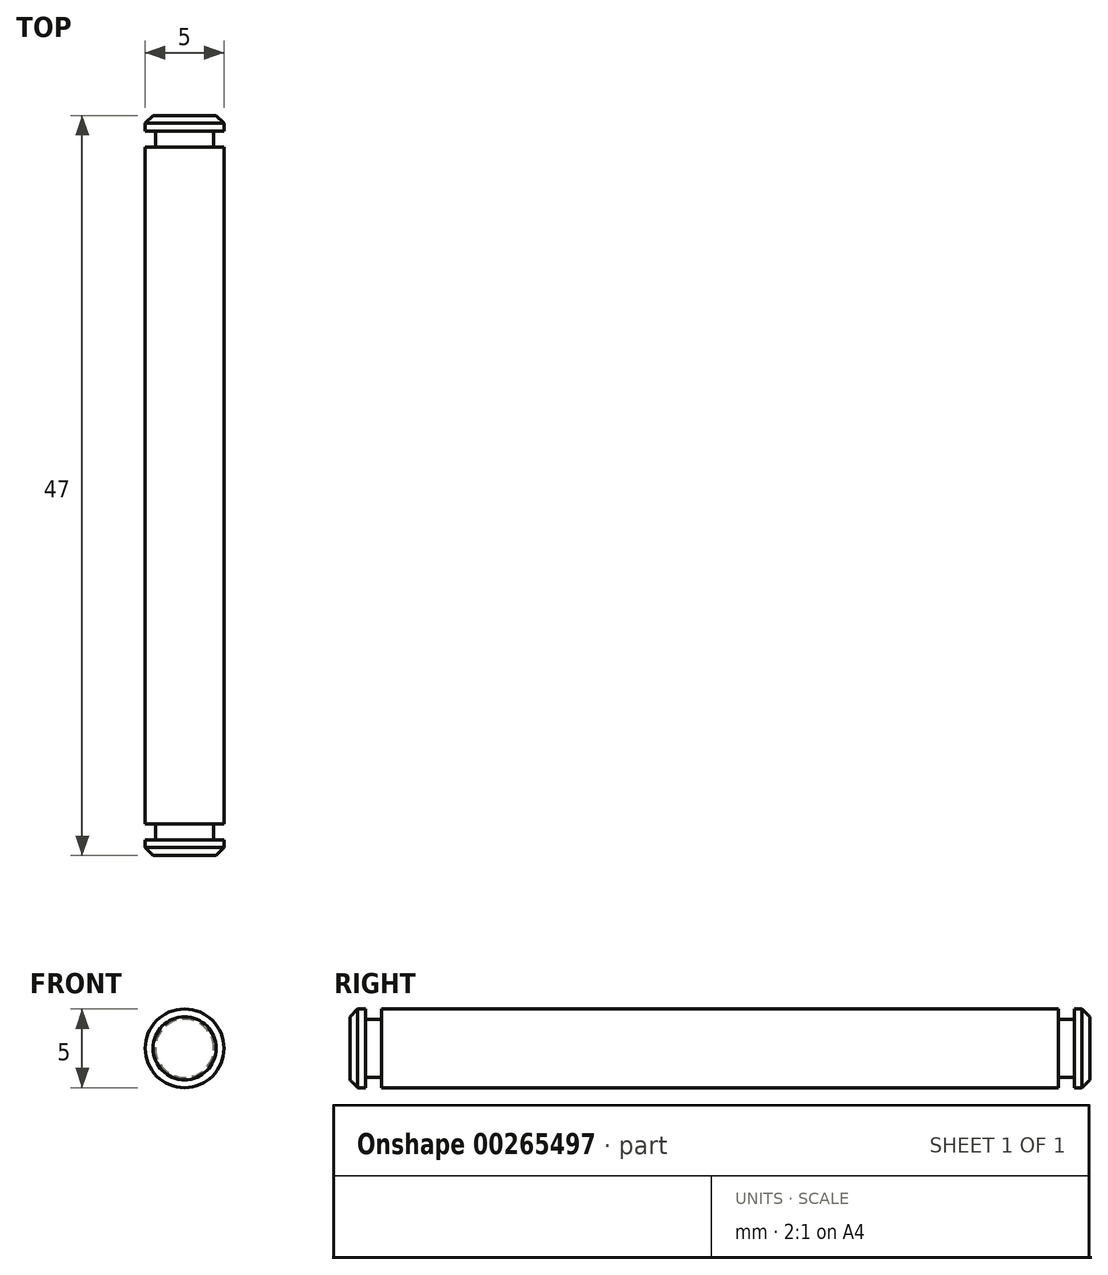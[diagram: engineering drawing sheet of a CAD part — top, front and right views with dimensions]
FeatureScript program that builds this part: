
annotation { "Feature Type Name" : "Feature", "Feature Type Description" : "" }
export const myFeature = defineFeature(function(context is Context, id is Id, definition is map)
    precondition{}
    {
        {
            var Q0;
            Q0=qCreatedBy(makeId("Front.planeOp"),FACE);
            var sketch = newSketch(context, id + "F0", { "sketchPlane" : qUnion([Q0])});
            skCircle(sketch, "E0", {"center": v(0, 0) * mm, "radius": 2.5 * mm});
            skSolve(sketch);
        }
        {
            var Q0;
            Q0=makeQuery(id+"F0.imprint","IMPRINT",FACE,{"disambiguationData":[TD([[makeQuery(id+"F0.imprint","IMPRINT",EDGE,{"derivedFrom":sQuery(id+"F0.wireOp",EDGE,"E0")}),1.0]])]});
            extrude(context, id + "F1", {"entities" : qUnion([Q0]), "depth" : 1 * mm});
        }
        {
            var Q0;
            Q0=makeQuery(id+"F1.opExtrude","CAP_FACE",FACE,{"disambiguationData":[OSD([sQuery(id+"F0.wireOp",EDGE,"E0")])],"isStart":false});
            var sketch = newSketch(context, id + "F2", { "sketchPlane" : qUnion([Q0])});
            skCircle(sketch, "E1", {"center": v(0, 0) * mm, "radius": 1.85 * mm});
            skSolve(sketch);
        }
        {
            var Q0;
            Q0=makeQuery(id+"F2.imprint","IMPRINT",FACE,{"disambiguationData":[TD([[makeQuery(id+"F2.imprint","IMPRINT",EDGE,{"derivedFrom":sQuery(id+"F2.wireOp",EDGE,"E1")}),1.0]])]});
            extrude(context, id + "F3", {"entities" : qUnion([Q0]), "operationType" : NewBodyOperationType.ADD, "depth" : 1 * mm});
        }
        {
            var Q0;
            Q0=makeQuery(id+"F3.opExtrude","CAP_FACE",FACE,{"disambiguationData":[OSD([sQuery(id+"F2.wireOp",EDGE,"E1")])],"isStart":false});
            var sketch = newSketch(context, id + "F4", { "sketchPlane" : qUnion([Q0])});
            skCircle(sketch, "E2", {"center": v(0, 0) * mm, "radius": 2.5 * mm});
            skSolve(sketch);
        }
        {
            var Q0;
            Q0=makeQuery(id+"F4.imprint","IMPRINT",FACE,{"disambiguationData":[TD([[makeQuery(id+"F4.imprint","IMPRINT",EDGE,{"derivedFrom":sQuery(id+"F4.wireOp",EDGE,"E2")}),1.0]])]});
            var Q1;
            Q1=makeQuery(id+"F4.imprint","IMPRINT",FACE,{"disambiguationData":[TD([[makeQuery(id+"F4.imprint","IMPRINT",EDGE,{"derivedFrom":makeQuery(id+"F3.opExtrude","CAP_EDGE",EDGE,{"disambiguationData":[OSD([sQuery(id+"F2.wireOp",EDGE,"E1")])],"isStart":false})}),1.0]])]});
            extrude(context, id + "F5", {"entities" : qUnion([Q0, Q1]), "operationType" : NewBodyOperationType.ADD, "depth" : 43 * mm});
        }
        {
            var Q0;
            Q0=makeQuery(id+"F5.opExtrude","CAP_FACE",FACE,{"disambiguationData":[OSD([sQuery(id+"F4.wireOp",EDGE,"E2")])],"isStart":false});
            var sketch = newSketch(context, id + "F6", { "sketchPlane" : qUnion([Q0])});
            skCircle(sketch, "E3", {"center": v(0, 0) * mm, "radius": 1.85 * mm});
            skSolve(sketch);
        }
        {
            var Q0;
            Q0=makeQuery(id+"F6.imprint","IMPRINT",FACE,{"disambiguationData":[TD([[makeQuery(id+"F6.imprint","IMPRINT",EDGE,{"derivedFrom":sQuery(id+"F6.wireOp",EDGE,"E3")}),1.0]])]});
            extrude(context, id + "F7", {"entities" : qUnion([Q0]), "operationType" : NewBodyOperationType.ADD, "depth" : 1 * mm});
        }
        {
            var Q0;
            Q0=makeQuery(id+"F7.opExtrude","CAP_FACE",FACE,{"disambiguationData":[OSD([sQuery(id+"F6.wireOp",EDGE,"E3")])],"isStart":false});
            var sketch = newSketch(context, id + "F8", { "sketchPlane" : qUnion([Q0])});
            skCircle(sketch, "E4", {"center": v(0, 0) * mm, "radius": 2.5 * mm});
            skSolve(sketch);
        }
        {
            var Q0;
            Q0=makeQuery(id+"F8.imprint","IMPRINT",FACE,{"disambiguationData":[TD([[makeQuery(id+"F8.imprint","IMPRINT",EDGE,{"derivedFrom":makeQuery(id+"F7.opExtrude","CAP_EDGE",EDGE,{"disambiguationData":[OSD([sQuery(id+"F6.wireOp",EDGE,"E3")])],"isStart":false})}),1.0]])]});
            var Q1;
            Q1=makeQuery(id+"F8.imprint","IMPRINT",FACE,{"disambiguationData":[TD([[makeQuery(id+"F8.imprint","IMPRINT",EDGE,{"derivedFrom":sQuery(id+"F8.wireOp",EDGE,"E4")}),1.0]])]});
            extrude(context, id + "F9", {"entities" : qUnion([Q0, Q1]), "operationType" : NewBodyOperationType.ADD, "depth" : 1 * mm});
        }
        {
            var Q0;
            Q0=makeQuery(id+"F9.opExtrude","CAP_EDGE",EDGE,{"disambiguationData":[OSD([sQuery(id+"F8.wireOp",EDGE,"E4")])],"isStart":false});
            var Q1;
            Q1=makeQuery(id+"F1.opExtrude","CAP_EDGE",EDGE,{"disambiguationData":[OSD([sQuery(id+"F0.wireOp",EDGE,"E0")])],"isStart":true});
            chamfer(context, id + "F10", {"entities" : qUnion([Q0, Q1]), "width" : 0.5 * mm, "tangentPropagation" : true});
        }
    });
